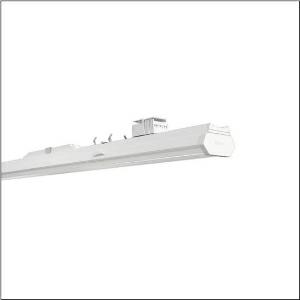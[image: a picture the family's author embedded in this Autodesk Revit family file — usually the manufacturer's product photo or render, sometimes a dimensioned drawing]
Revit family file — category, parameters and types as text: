
# Revit family: licross_r__11_protected_mo_51td12mn4axg_dbc1
name_source: partatom
category: Lighting Fixtures
units: mm (PartAtom-declared; Revit-internal decimal feet)

## family parameters
Cut with Voids When Loaded = No
Host = Face
Light Source = No
Part Type = Normal
Room Calculation Point = No
Round Connector Dimension = Use Diameter
Shared = No

## types (1)
- --- (1 x LED, 10020 lm, 55.3 W, 4000K)
    Apparent Load = 55 VA
    CIE Flux Codes = 73 92 98 99 100
    Color Rendering = 80
    Color Temperature = 4000K
    Default Elevation = 1800 mm
    Description = Licross® 11 Protected MO, luminaire insert, of sheet steel, galvanised, coil coated, white, length: 1.500mm, width: 90mm, height: 101mm, LED rated luminous flux: 10.030lm, light colour: 840, control gear: ON/OFF Multilumen, control gear: ECG Multilumen, with plug, 3-pole, with phase selection, mains connection: 220..240V, AC, 50/60Hz, halogen-free wiring, primary light control with lens, of plastic, primary optical cover: cover, of PMMA, light emission: direct with ceiling illumination distribution, primary light characteristic: symmetric, protection rating (complete): IP54, insulation class (complete): insulation class I (protective earthing), certification: CE, ENEC, VDE, UKCA, protection symbol: D if used in an environment with non-conductive dust loads with corresponding accessories, impact resistance: IK06, permissible ambient temperature for indoor applications: -35..+40°C, corresponds to IFS (International Featured Standards) requirements for safety and quality in the food industry, reducing of maximum allowable ambient temperature of 5°C with ceiling mounting, LABS conformity tested according to VDMA 24364:2018-05, packaging unit: 1 piece
    Height = 92 mm
    Lamp = 1 x LED
    Lamp Light Flux = 10020 lm
    Lamp Power = 55.3 W
    Lamp count = 1
    Length = 1500 mm
    Luminous efficacy = 181 lm/W
    Manufacturer = Siteco
    ModVariant = No
    Model = 51TD12MN4AXG
    Mounting Place = Ceiling
    Mounting Type = Pendant
    Number of Poles = 1
    OnlyDefault = Yes
    Power Factor = 1
    Product Name = Licross® 11 Protected MO
    Product group = luminaire insert
    ProductGroupID = 902
    Protection Class = Protection class I
    Protection Degree = IP 54
    RLX_Detail_Level = 1
    RlxData = <blob elided: 22073 chars, md5=c7925326>
    Socket = socket
    Standby Power = 0 W
    System Light Flux = 10020 lm
    System Power = 55 W
    Type Comments = factory setting: luminous flux: 100 % | (A | C | E) | 126 mA
    Type Image = l_1256145.jpg
    URL = http://relux.com
    VarID = @adj_003871
    Voltage = 0 V
    Weight = 0.00 kg
    Width = 88 mm

## geometry (parser evidence)
native form markers: Blend x4, Sweep x11
no freeform markers — native parametric forms only
